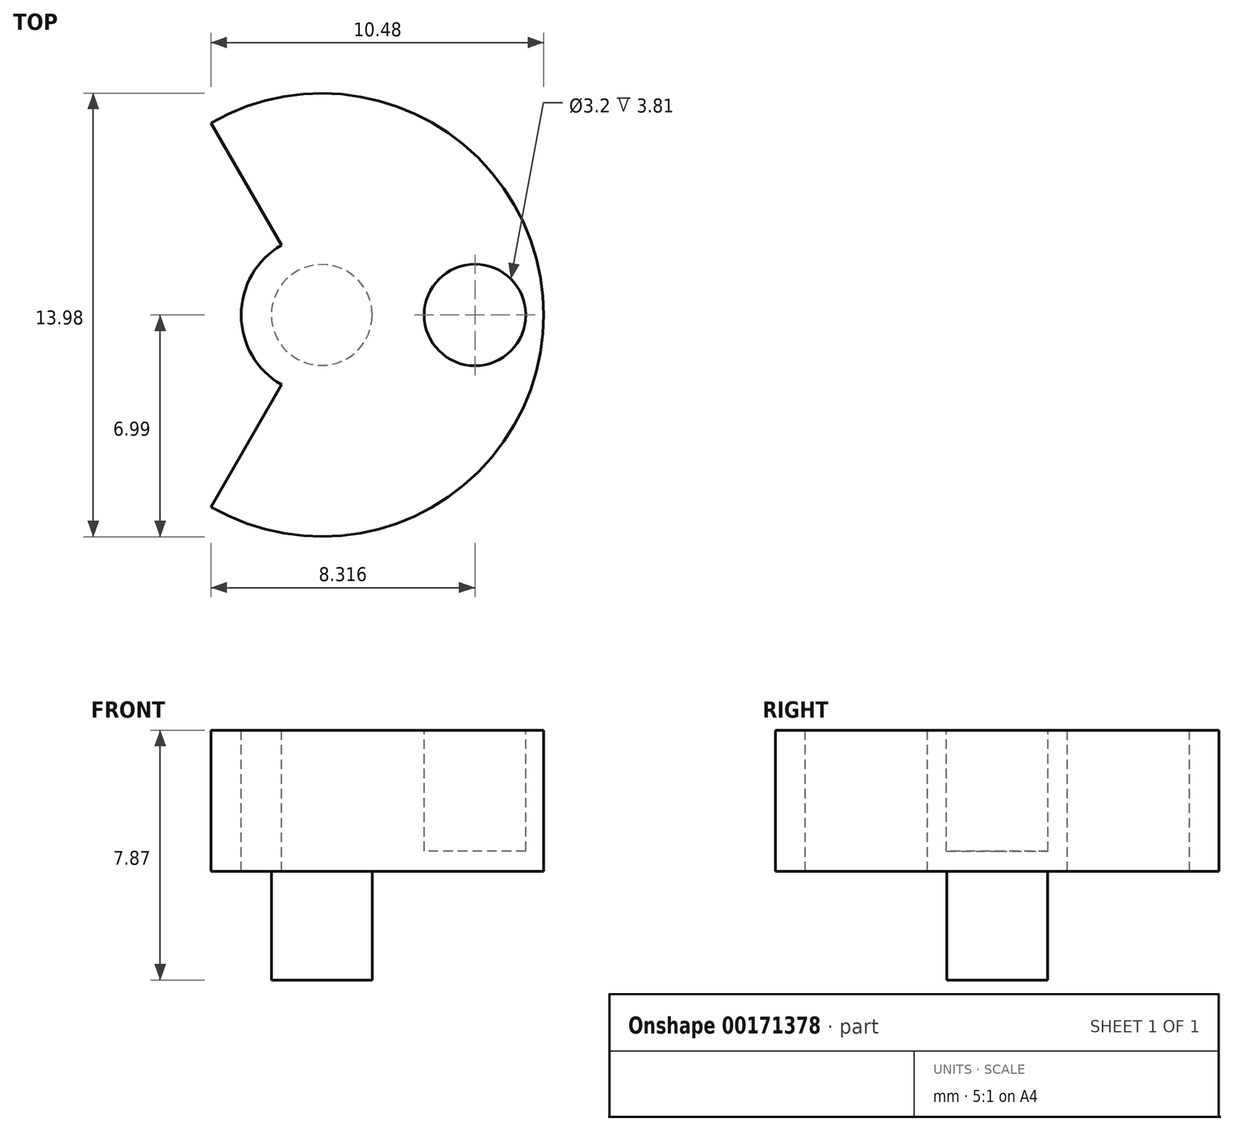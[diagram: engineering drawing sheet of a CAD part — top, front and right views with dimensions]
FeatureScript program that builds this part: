
annotation { "Feature Type Name" : "Feature", "Feature Type Description" : "" }
export const myFeature = defineFeature(function(context is Context, id is Id, definition is map)
    precondition{}
    {
        {
            var Q0;
            Q0=qCreatedBy(makeId("Top.planeOp"),FACE);
            var sketch = newSketch(context, id + "F0", { "sketchPlane" : qUnion([Q0])});
            skCircle(sketch, "E0", {"center": v(0, 0) * mm, "radius": 6.99 * mm});
            skCircle(sketch, "E1", {"center": v(4.83, 0) * mm, "radius": 1.6 * mm});
            skCircle(sketch, "E2", {"center": v(0, 0) * mm, "radius": 2.54 * mm});
            skLineSegment(sketch, "E3", {"start": v(0, 0) * mm, "end": v(-3.5, 6.05) * mm});
            skLineSegment(sketch, "E4", {"start": v(0, 0) * mm, "end": v(-3.5, -6.05) * mm});
            skSolve(sketch);
        }
        {
            var Q0;
            Q0=makeQuery(id+"F0.imprint","IMPRINT",FACE,{"disambiguationData":[TD([[makeQuery(id+"F0.imprint","IMPRINT",EDGE,{"derivedFrom":sQuery(id+"F0.wireOp",EDGE,"E1")}),-1.0]])]});
            var Q1;
            {var subQ0=sQuery(id+"F0.wireOp",EDGE,"E3");var subQ1=sQuery(id+"F0.wireOp",EDGE,"E2");var subQ2=makeQuery(id+"F0.imprint","INTERSECT",VERTEX,{"derivedFrom":[subQ1,subQ0]});Q1=makeQuery(id+"F0.imprint","IMPRINT",FACE,{"disambiguationData":[TD([[makeQuery(id+"F0.imprint","IMPRINT",EDGE,{"disambiguationData":[TD([[subQ2,1.0]])],"derivedFrom":subQ1}),1.0]])]});}
            var Q2;
            Q2=makeQuery(id+"F0.imprint","IMPRINT",FACE,{"disambiguationData":[TD([[makeQuery(id+"F0.imprint","IMPRINT",EDGE,{"derivedFrom":sQuery(id+"F0.wireOp",EDGE,"E1")}),1.0]])]});
            var Q3;
            {var subQ0=sQuery(id+"F0.wireOp",EDGE,"E3");var subQ1=sQuery(id+"F0.wireOp",EDGE,"E2");var subQ2=makeQuery(id+"F0.imprint","INTERSECT",VERTEX,{"derivedFrom":[subQ1,subQ0]});Q3=makeQuery(id+"F0.imprint","IMPRINT",FACE,{"disambiguationData":[TD([[makeQuery(id+"F0.imprint","IMPRINT",EDGE,{"disambiguationData":[TD([[subQ2,-1.0]])],"derivedFrom":subQ1}),1.0]])]});}
            extrude(context, id + "F1", {"entities" : qUnion([Q0, Q1, Q2, Q3]), "oppositeDirection" : true, "depth" : 4.44 * mm});
        }
        {
            var Q0;
            Q0=makeQuery(id+"F0.imprint","IMPRINT",FACE,{"disambiguationData":[TD([[makeQuery(id+"F0.imprint","IMPRINT",EDGE,{"derivedFrom":sQuery(id+"F0.wireOp",EDGE,"E1")}),1.0]])]});
            extrude(context, id + "F2", {"entities" : qUnion([Q0]), "operationType" : NewBodyOperationType.REMOVE, "oppositeDirection" : true, "depth" : 3.8 * mm});
        }
        {
            var Q0;
            Q0=makeQuery(id+"F1.opExtrude","CAP_FACE",FACE,{"disambiguationData":[OSD([sQuery(id+"F0.wireOp",EDGE,"E0"),sQuery(id+"F0.wireOp",EDGE,"E2"),sQuery(id+"F0.wireOp",EDGE,"E3"),sQuery(id+"F0.wireOp",EDGE,"E4")])],"isStart":false});
            var sketch = newSketch(context, id + "F3", { "sketchPlane" : qUnion([Q0])});
            skCircle(sketch, "E5", {"center": v(0, 0) * mm, "radius": 1.59 * mm});
            skSolve(sketch);
        }
        {
            var Q0;
            Q0=makeQuery(id+"F3.imprint","IMPRINT",FACE,{"disambiguationData":[TD([[makeQuery(id+"F3.imprint","IMPRINT",EDGE,{"derivedFrom":sQuery(id+"F3.wireOp",EDGE,"E5")}),1.0]])]});
            extrude(context, id + "F4", {"entities" : qUnion([Q0]), "operationType" : NewBodyOperationType.ADD, "depth" : 3.43 * mm});
        }
    });
